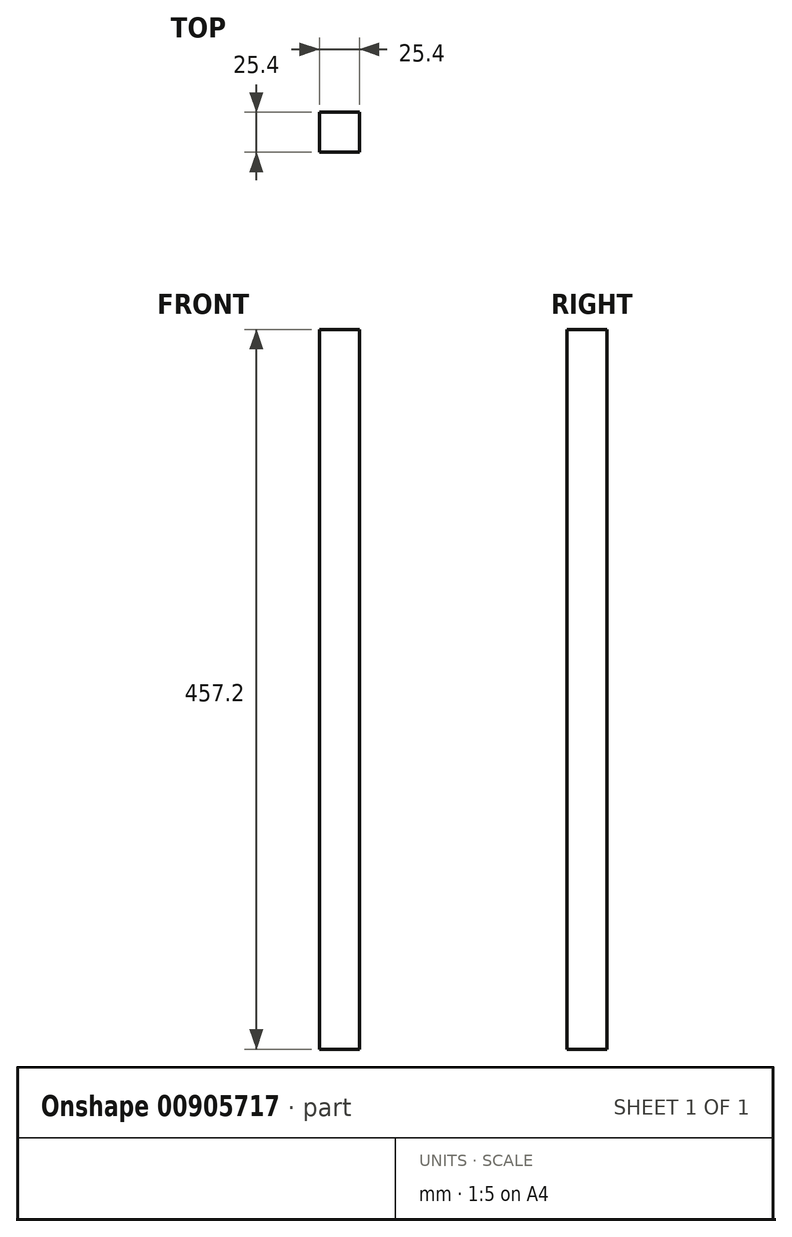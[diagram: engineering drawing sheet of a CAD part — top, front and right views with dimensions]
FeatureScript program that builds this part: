
annotation { "Feature Type Name" : "Feature", "Feature Type Description" : "" }
export const myFeature = defineFeature(function(context is Context, id is Id, definition is map)
    precondition{}
    {
        {
            var Q0;
            Q0=qCreatedBy(makeId("Right.planeOp"),FACE);
            var sketch = newSketch(context, id + "F0", { "sketchPlane" : qUnion([Q0])});
            skLineSegment(sketch, "E0.bottom", {"start": v(-18.63, 463.06) * mm, "end": v(6.77, 463.06) * mm});
            skLineSegment(sketch, "E0.top", {"start": v(-18.63, 5.86) * mm, "end": v(6.77, 5.86) * mm});
            skLineSegment(sketch, "E0.left", {"start": v(-18.63, 463.06) * mm, "end": v(-18.63, 5.86) * mm});
            skLineSegment(sketch, "E0.right", {"start": v(6.77, 463.06) * mm, "end": v(6.77, 5.86) * mm});
            skSolve(sketch);
        }
        {
            var Q0;
            Q0=makeQuery(id+"F0.imprint","IMPRINT",FACE,{"disambiguationData":[TD([[makeQuery(id+"F0.imprint","IMPRINT",EDGE,{"derivedFrom":sQuery(id+"F0.wireOp",EDGE,"E0.bottom")}),-1.0]])]});
            extrude(context, id + "F1", {"entities" : qUnion([Q0]), "depth" : 25.4 * mm, "offsetDistance" : 25.4 * mm});
        }
    });
